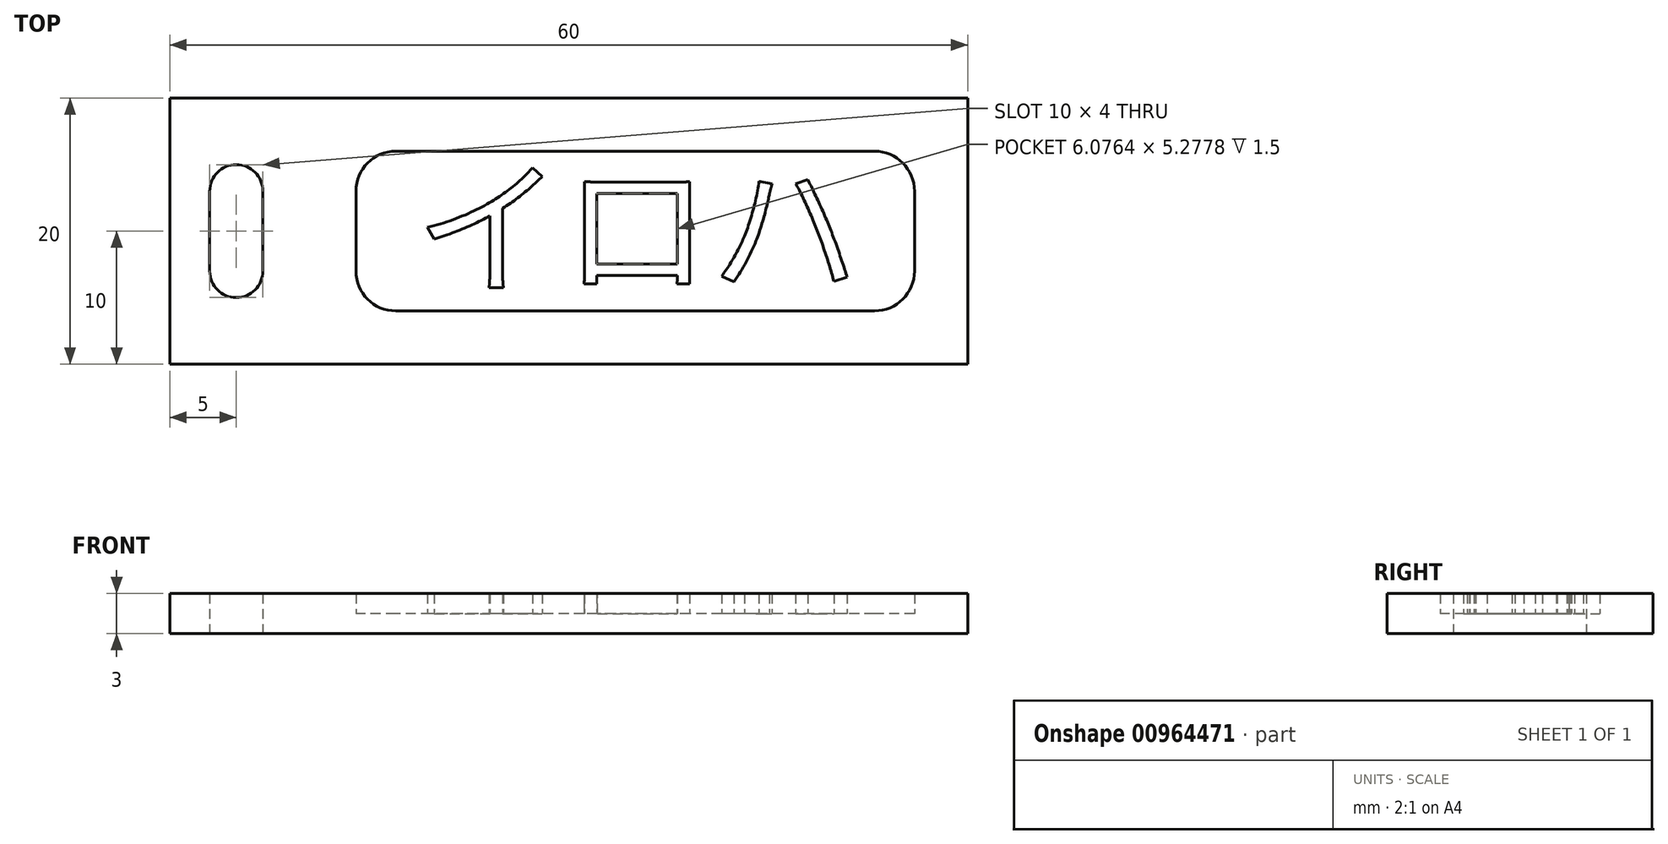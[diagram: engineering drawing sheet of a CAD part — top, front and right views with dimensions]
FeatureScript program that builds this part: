
annotation { "Feature Type Name" : "Feature", "Feature Type Description" : "" }
export const myFeature = defineFeature(function(context is Context, id is Id, definition is map)
    precondition{}
    {
        {
            var Q0;
            Q0=qCreatedBy(makeId("Top.planeOp"),FACE);
            var sketch = newSketch(context, id + "F0", { "sketchPlane" : qUnion([Q0])});
            skLineSegment(sketch, "E0.bottom", {"start": v(25, 10) * mm, "end": v(-25, 10) * mm});
            skLineSegment(sketch, "E0.top", {"start": v(25, -10) * mm, "end": v(-25, -10) * mm});
            skLineSegment(sketch, "E0.left", {"start": v(25, 10) * mm, "end": v(25, -10) * mm});
            skLineSegment(sketch, "E0.right", {"start": v(-25, 10) * mm, "end": v(-25, -10) * mm});
            skPoint(sketch, "E0.middle", {"position": v(0, 0) * mm});
            skLineSegment(sketch, "E1.bottom", {"start": v(-25, 10) * mm, "end": v(-35, 10) * mm});
            skLineSegment(sketch, "E1.top", {"start": v(-25, -10) * mm, "end": v(-35, -10) * mm});
            skLineSegment(sketch, "E1.right", {"start": v(-35, 10) * mm, "end": v(-35, -10) * mm});
            skPoint(sketch, "E1.middle", {"position": v(-30, 0) * mm});
            skLineSegment(sketch, "E2.bottom", {"start": v(-30, 5) * mm, "end": v(-30, 5) * mm});
            skLineSegment(sketch, "E2.top", {"start": v(-30, -5) * mm, "end": v(-30, -5) * mm});
            skLineSegment(sketch, "E2.left", {"start": v(-28, 3) * mm, "end": v(-28, -3) * mm});
            skLineSegment(sketch, "E2.right", {"start": v(-32, 3) * mm, "end": v(-32, -3) * mm});
            skPoint(sketch, "E3.visualSharp", {"position": v(-32, 5) * mm});
            skArc(sketch, "E3.filletArc", {"start": v(-30, 5) * mm, "mid": v(-31.41, 4.41) * mm, "end": v(-32, 3) * mm});
            skPoint(sketch, "E4.visualSharp", {"position": v(-28, 5) * mm});
            skArc(sketch, "E4.filletArc", {"start": v(-28, 3) * mm, "mid": v(-28.59, 4.41) * mm, "end": v(-30, 5) * mm});
            skPoint(sketch, "E5.visualSharp", {"position": v(-32, -5) * mm});
            skArc(sketch, "E5.filletArc", {"start": v(-32, -3) * mm, "mid": v(-31.41, -4.41) * mm, "end": v(-30, -5) * mm});
            skPoint(sketch, "E6.visualSharp", {"position": v(-28, -5) * mm});
            skArc(sketch, "E6.filletArc", {"start": v(-30, -5) * mm, "mid": v(-28.59, -4.41) * mm, "end": v(-28, -3) * mm});
            skSolve(sketch);
        }
        {
            var Q0;
            Q0 = qSketchRegion(id + "F0", true);
            extrude(context, id + "F1", {"entities" : qUnion([Q0]), "depth" : 3 * mm, "offsetDistance" : 25 * mm});
        }
        {
            var Q0;
            Q0=qCreatedBy(makeId("Top.planeOp"),FACE);
            var sketch = newSketch(context, id + "F2", { "sketchPlane" : qUnion([Q0])});
            skLineSegment(sketch, "E7.bottom", {"start": v(18, 6) * mm, "end": v(-18, 6) * mm});
            skLineSegment(sketch, "E7.top", {"start": v(18, -6) * mm, "end": v(-18, -6) * mm});
            skLineSegment(sketch, "E7.left", {"start": v(21, 3) * mm, "end": v(21, -3) * mm});
            skLineSegment(sketch, "E7.right", {"start": v(-21, 3) * mm, "end": v(-21, -3) * mm});
            skPoint(sketch, "E7.middle", {"position": v(0, 0) * mm});
            skPoint(sketch, "E8.visualSharp", {"position": v(-21, 6) * mm});
            skArc(sketch, "E8.filletArc", {"start": v(-18, 6) * mm, "mid": v(-20.12, 5.12) * mm, "end": v(-21, 3) * mm});
            skPoint(sketch, "E9.visualSharp", {"position": v(21, 6) * mm});
            skArc(sketch, "E9.filletArc", {"start": v(21, 3) * mm, "mid": v(20.12, 5.12) * mm, "end": v(18, 6) * mm});
            skPoint(sketch, "E10.visualSharp", {"position": v(21, -6) * mm});
            skArc(sketch, "E10.filletArc", {"start": v(18, -6) * mm, "mid": v(20.12, -5.12) * mm, "end": v(21, -3) * mm});
            skPoint(sketch, "E11.visualSharp", {"position": v(-21, -6) * mm});
            skArc(sketch, "E11.filletArc", {"start": v(-21, -3) * mm, "mid": v(-20.12, -5.12) * mm, "end": v(-18, -6) * mm});
            skSolve(sketch);
        }
        {
            var Q0;
            Q0 = qSketchRegion(id + "F2", true);
            extrude(context, id + "F3", {"entities" : qUnion([Q0]), "depth" : 3 * mm, "offsetDistance" : 25 * mm});
        }
        {
            var Q0;
            Q0=makeQuery(id+"F3.opExtrude","SWEPT_BODY",BODY,{"disambiguationData":[OSD([sQuery(id+"F2.wireOp",EDGE,"E7.bottom"),sQuery(id+"F2.wireOp",EDGE,"E7.top"),sQuery(id+"F2.wireOp",EDGE,"E7.left"),sQuery(id+"F2.wireOp",EDGE,"E7.right"),sQuery(id+"F2.wireOp",EDGE,"E8.filletArc"),sQuery(id+"F2.wireOp",EDGE,"E9.filletArc"),sQuery(id+"F2.wireOp",EDGE,"E10.filletArc"),sQuery(id+"F2.wireOp",EDGE,"E11.filletArc")])]});
            transform(context, id + "F4", {"entities" : qUnion([Q0]), "transformType" : TransformType.TRANSLATION_3D, "dx" : 0 * mm, "dy" : 0 * mm, "dz" : 1.5 * mm, "makeCopy" : false});
        }
        {
            var Q0;
            Q0=makeQuery(id+"F3.opExtrude","SWEPT_BODY",BODY,{"disambiguationData":[OSD([sQuery(id+"F2.wireOp",EDGE,"E7.bottom"),sQuery(id+"F2.wireOp",EDGE,"E7.top"),sQuery(id+"F2.wireOp",EDGE,"E7.left"),sQuery(id+"F2.wireOp",EDGE,"E7.right"),sQuery(id+"F2.wireOp",EDGE,"E8.filletArc"),sQuery(id+"F2.wireOp",EDGE,"E9.filletArc"),sQuery(id+"F2.wireOp",EDGE,"E10.filletArc"),sQuery(id+"F2.wireOp",EDGE,"E11.filletArc")])]});
            var Q1;
            Q1=makeQuery(id+"F1.opExtrude","SWEPT_BODY",BODY,{"disambiguationData":[OSD([sQuery(id+"F0.wireOp",EDGE,"E0.bottom"),sQuery(id+"F0.wireOp",EDGE,"E0.top"),sQuery(id+"F0.wireOp",EDGE,"E0.left"),sQuery(id+"F0.wireOp",EDGE,"E1.bottom"),sQuery(id+"F0.wireOp",EDGE,"E1.top"),sQuery(id+"F0.wireOp",EDGE,"E1.right"),sQuery(id+"F0.wireOp",EDGE,"E2.left"),sQuery(id+"F0.wireOp",EDGE,"E2.right"),sQuery(id+"F0.wireOp",EDGE,"E3.filletArc"),sQuery(id+"F0.wireOp",EDGE,"E4.filletArc"),sQuery(id+"F0.wireOp",EDGE,"E5.filletArc"),sQuery(id+"F0.wireOp",EDGE,"E6.filletArc")])]});
            booleanBodies(context, id + "F5", {"operationType" : BooleanOperationType.SUBTRACTION, "tools" : qUnion([Q0]), "targets" : qUnion([Q1])});
        }
        {
            var Q0;
            Q0=qCreatedBy(makeId("Top.planeOp"),FACE);
            var sketch = newSketch(context, id + "F6", { "sketchPlane" : qUnion([Q0])});
            skText(sketch, "E12", { "text": "イロハ", "fontName": "NotoSansCJKjp-Regular.otf"});
            const initialGuessF6  = {"E12": [-0.01656, -0.0039, 1, 0, 0.008]};
            skSetInitialGuess(sketch, initialGuessF6);
            skSolve(sketch);
        }
        {
            var Q0;
            Q0 = qSketchRegion(id + "F6", true);
            extrude(context, id + "F7", {"entities" : qUnion([Q0]), "operationType" : NewBodyOperationType.ADD, "depth" : 3 * mm, "offsetDistance" : 25 * mm});
        }
    });
